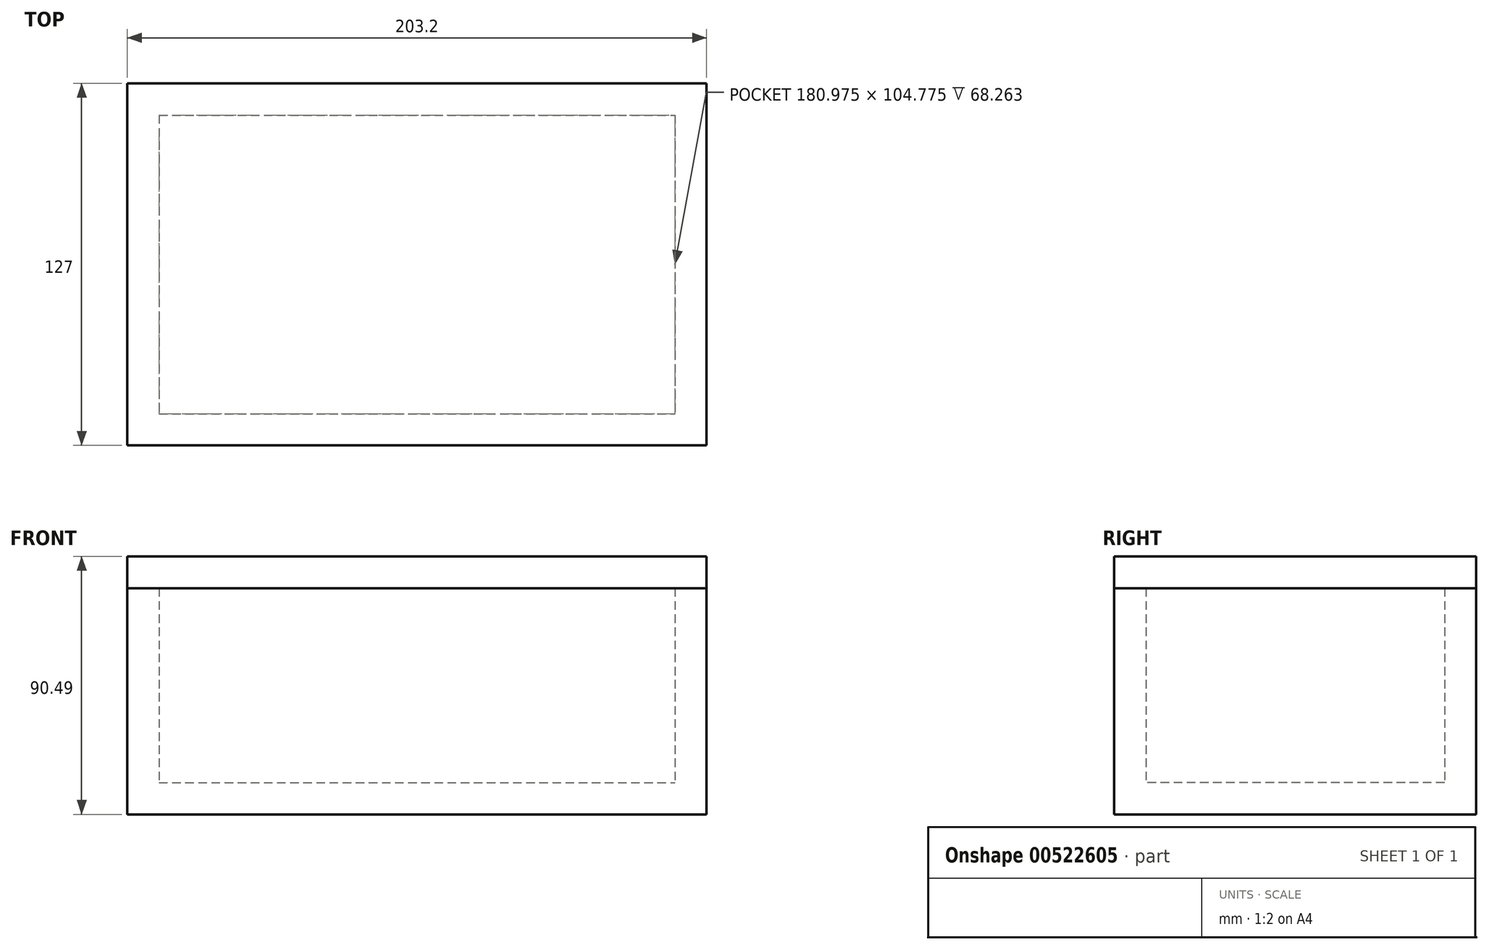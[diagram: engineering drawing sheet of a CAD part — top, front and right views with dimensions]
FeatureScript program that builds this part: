
annotation { "Feature Type Name" : "Feature", "Feature Type Description" : "" }
export const myFeature = defineFeature(function(context is Context, id is Id, definition is map)
    precondition{}
    {
        {
            var Q0;
            Q0=qCreatedBy(makeId("Top.planeOp"),FACE);
            var sketch = newSketch(context, id + "F0", { "sketchPlane" : qUnion([Q0])});
            skLineSegment(sketch, "E0.bottom", {"start": v(-101.6, 63.5) * mm, "end": v(101.6, 63.5) * mm});
            skLineSegment(sketch, "E0.top", {"start": v(-101.6, -63.5) * mm, "end": v(101.6, -63.5) * mm});
            skLineSegment(sketch, "E0.left", {"start": v(-101.6, 63.5) * mm, "end": v(-101.6, -63.5) * mm});
            skLineSegment(sketch, "E0.right", {"start": v(101.6, 63.5) * mm, "end": v(101.6, -63.5) * mm});
            skPoint(sketch, "E0.middle", {"position": v(0, 0) * mm});
            skSolve(sketch);
        }
        {
            var Q0;
            Q0 = qSketchRegion(id + "F0", true);
            extrude(context, id + "F1", {"entities" : qUnion([Q0]), "depth" : 79.38 * mm, "offsetDistance" : 25.4 * mm});
        }
        {
            var Q0;
            Q0=makeQuery(id+"F1.opExtrude","CAP_FACE",FACE,{"disambiguationData":[OSD([sQuery(id+"F0.wireOp",EDGE,"E0.bottom"),sQuery(id+"F0.wireOp",EDGE,"E0.top"),sQuery(id+"F0.wireOp",EDGE,"E0.left"),sQuery(id+"F0.wireOp",EDGE,"E0.right")])],"isStart":false});
            shell(context, id + "F2", {"entities" : qUnion([Q0]), "thickness" : 11.1 * mm});
        }
        {
            var Q0;
            Q0=makeQuery(id+"F1.opExtrude","CAP_FACE",FACE,{"disambiguationData":[OSD([sQuery(id+"F0.wireOp",EDGE,"E0.bottom"),sQuery(id+"F0.wireOp",EDGE,"E0.top"),sQuery(id+"F0.wireOp",EDGE,"E0.left"),sQuery(id+"F0.wireOp",EDGE,"E0.right")])],"isStart":false});
            var sketch = newSketch(context, id + "F3", { "sketchPlane" : qUnion([Q0])});
            skLineSegment(sketch, "E1.bottom", {"start": v(-101.6, 63.5) * mm, "end": v(101.6, 63.5) * mm});
            skLineSegment(sketch, "E1.top", {"start": v(-101.6, -63.5) * mm, "end": v(101.6, -63.5) * mm});
            skLineSegment(sketch, "E1.left", {"start": v(-101.6, 63.5) * mm, "end": v(-101.6, -63.5) * mm});
            skLineSegment(sketch, "E1.right", {"start": v(101.6, 63.5) * mm, "end": v(101.6, -63.5) * mm});
            skSolve(sketch);
        }
        {
            var Q0;
            Q0 = qSketchRegion(id + "F3", true);
            extrude(context, id + "F4", {"entities" : qUnion([Q0]), "depth" : 11.1 * mm, "offsetDistance" : 25.4 * mm});
        }
    });
